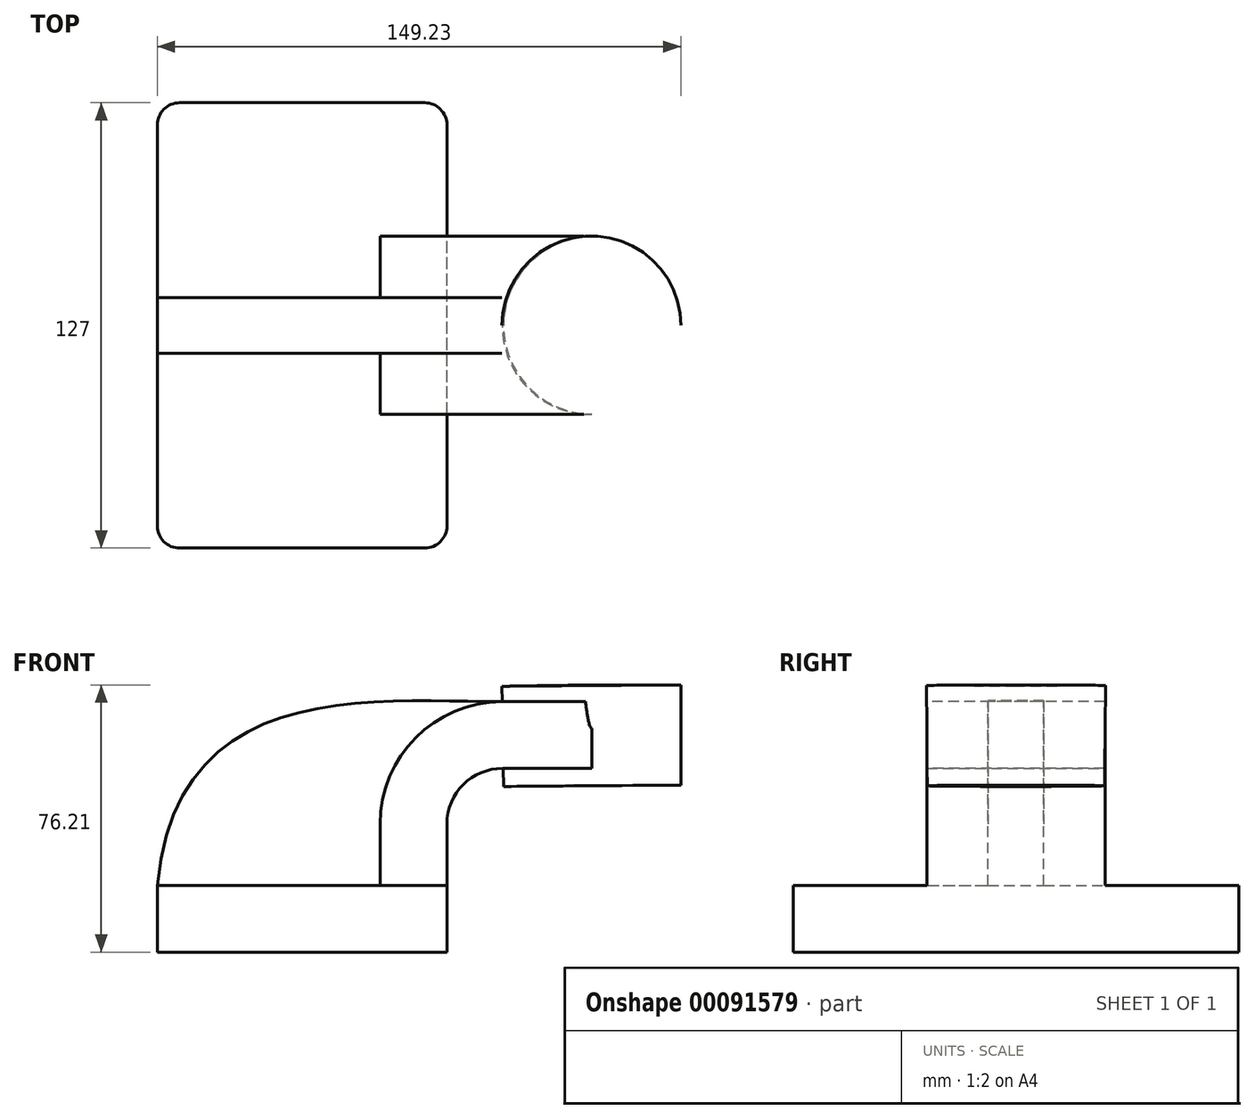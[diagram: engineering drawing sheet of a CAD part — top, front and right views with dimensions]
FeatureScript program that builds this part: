
annotation { "Feature Type Name" : "Feature", "Feature Type Description" : "" }
export const myFeature = defineFeature(function(context is Context, id is Id, definition is map)
    precondition{}
    {
        {
            var Q0;
            Q0=qCreatedBy(makeId("Front.planeOp"),FACE);
            var sketch = newSketch(context, id + "F0", { "sketchPlane" : qUnion([Q0])});
            skLineSegment(sketch, "E0.bottom", {"start": v(41.27, 9.53) * mm, "end": v(-41.28, 9.53) * mm});
            skLineSegment(sketch, "E0.top", {"start": v(41.28, -9.52) * mm, "end": v(-41.27, -9.52) * mm});
            skLineSegment(sketch, "E0.left", {"start": v(41.28, 9.53) * mm, "end": v(41.28, -9.52) * mm});
            skLineSegment(sketch, "E0.right", {"start": v(-41.28, 9.53) * mm, "end": v(-41.27, -9.52) * mm});
            skPoint(sketch, "E0.middle", {"position": v(0, 0) * mm});
            skLineSegment(sketch, "E1.bottom", {"start": v(57.15, 38.1) * mm, "end": v(107.95, 38.1) * mm});
            skLineSegment(sketch, "E1.top", {"start": v(57.15, 66.68) * mm, "end": v(107.95, 66.68) * mm});
            skLineSegment(sketch, "E1.left", {"start": v(57.15, 38.1) * mm, "end": v(57.15, 66.68) * mm});
            skLineSegment(sketch, "E1.right", {"start": v(107.95, 38.1) * mm, "end": v(107.95, 66.68) * mm});
            skPoint(sketch, "E1.middle", {"position": v(82.55, 52.39) * mm});
            skLineSegment(sketch, "E2", {"start": v(41.27, 9.53) * mm, "end": v(41.27, 27) * mm});
            skArc(sketch, "E3", {"start": v(41.27, 27) * mm, "mid": v(45.92, 38.23) * mm, "end": v(57.15, 42.88) * mm});
            skLineSegment(sketch, "E4", {"start": v(57.15, 42.88) * mm, "end": v(82.68, 42.88) * mm});
            skLineSegment(sketch, "E5.0", {"start": v(57.15, 61.93) * mm, "end": v(88.89, 61.93) * mm});
            skArc(sketch, "E5.1", {"start": v(22.22, 27) * mm, "mid": v(32.45, 51.7) * mm, "end": v(57.15, 61.93) * mm});
            skLineSegment(sketch, "E5.2", {"start": v(22.22, 9.53) * mm, "end": v(22.22, 27) * mm});
            skFitSpline(sketch, "E6", {"points": [v(-41.28, 9.53) * mm, v(57.15, 61.93) * mm], "startDerivative": vector(16.73, 179.78) * mm, "endDerivative": vector(106.88, 0.4) * mm});
            skLineSegment(sketch, "E7", {"start": v(82.45, 66.68) * mm, "end": v(82.68, 38.1) * mm});
            skSolve(sketch);
        }
        {
            var Q0;
            Q0=makeQuery(id+"F0.imprint","IMPRINT",FACE,{"disambiguationData":[TD([[makeQuery(id+"F0.imprint","IMPRINT",EDGE,{"derivedFrom":sQuery(id+"F0.wireOp",EDGE,"E0.top")}),-1.0]])]});
            extrude(context, id + "F1", {"entities" : qUnion([Q0]), "endBound" : BoundingType.SYMMETRIC, "depth" : 127 * mm});
        }
        {
            var Q0;
            {var subQ1=sQuery(id+"F0.wireOp",EDGE,"E2");Q0=makeQuery(id+"F0.imprint","IMPRINT",FACE,{"disambiguationData":[TD([[makeQuery(id+"F0.imprint","IMPRINT",EDGE,{"derivedFrom":subQ1}),1.0]])]});}
            var Q1;
            {var subQ0=sQuery(id+"F0.wireOp",EDGE,"E4");var subQ5=sQuery(id+"F0.wireOp",EDGE,"E7");var subQ6=makeQuery(id+"F0.imprint","INTERSECT",VERTEX,{"derivedFrom":[subQ0,subQ5]});Q1=makeQuery(id+"F0.imprint","IMPRINT",FACE,{"disambiguationData":[TD([[makeQuery(id+"F0.imprint","IMPRINT",EDGE,{"disambiguationData":[TD([[subQ6,1.0]])],"derivedFrom":subQ5}),-1.0]])]});}
            extrude(context, id + "F2", {"entities" : qUnion([Q0, Q1]), "operationType" : NewBodyOperationType.ADD, "endBound" : BoundingType.SYMMETRIC, "depth" : 50.8 * mm});
        }
        {
            var Q0;
            {var subQ3=sQuery(id+"F0.wireOp",EDGE,"E5.2");Q0=makeQuery(id+"F0.imprint","IMPRINT",FACE,{"disambiguationData":[TD([[makeQuery(id+"F0.imprint","IMPRINT",EDGE,{"derivedFrom":subQ3}),1.0]])]});}
            extrude(context, id + "F3", {"entities" : qUnion([Q0]), "operationType" : NewBodyOperationType.ADD, "endBound" : BoundingType.SYMMETRIC, "depth" : 15.88 * mm});
        }
        {
            var Q0;
            {var subQ0=sQuery(id+"F0.wireOp",EDGE,"E1.right");Q0=makeQuery(id+"F0.imprint","IMPRINT",FACE,{"disambiguationData":[TD([[makeQuery(id+"F0.imprint","IMPRINT",EDGE,{"derivedFrom":subQ0}),1.0]])]});}
            var Q1;
            Q1=sQuery(id+"F0.wireOp",EDGE,"E7");
            revolve(context, id + "F4", {"operationType" : NewBodyOperationType.ADD, "entities" : qUnion([Q0]), "axis" : qUnion([Q1]), "revolveType" : RevolveType.FULL});
        }
        {
            var Q0;
            Q0=makeQuery(id+"F1.opExtrude","CAP_EDGE",EDGE,{"disambiguationData":[OSD([sQuery(id+"F0.wireOp",EDGE,"E0.left")])],"isStart":false});
            var Q1;
            Q1=makeQuery(id+"F1.opExtrude","CAP_EDGE",EDGE,{"disambiguationData":[OSD([sQuery(id+"F0.wireOp",EDGE,"E0.right")])],"isStart":false});
            var Q2;
            Q2=makeQuery(id+"F1.opExtrude","CAP_EDGE",EDGE,{"disambiguationData":[OSD([sQuery(id+"F0.wireOp",EDGE,"E0.left")])],"isStart":true});
            var Q3;
            Q3=makeQuery(id+"F1.opExtrude","CAP_EDGE",EDGE,{"disambiguationData":[OSD([sQuery(id+"F0.wireOp",EDGE,"E0.right")])],"isStart":true});
            fillet(context, id + "F5", {"entities" : qUnion([Q0, Q1, Q2, Q3]), "radius" : 6.35 * mm, "tangentPropagation" : true, "allowEdgeOverflow" : false});
        }
    });
